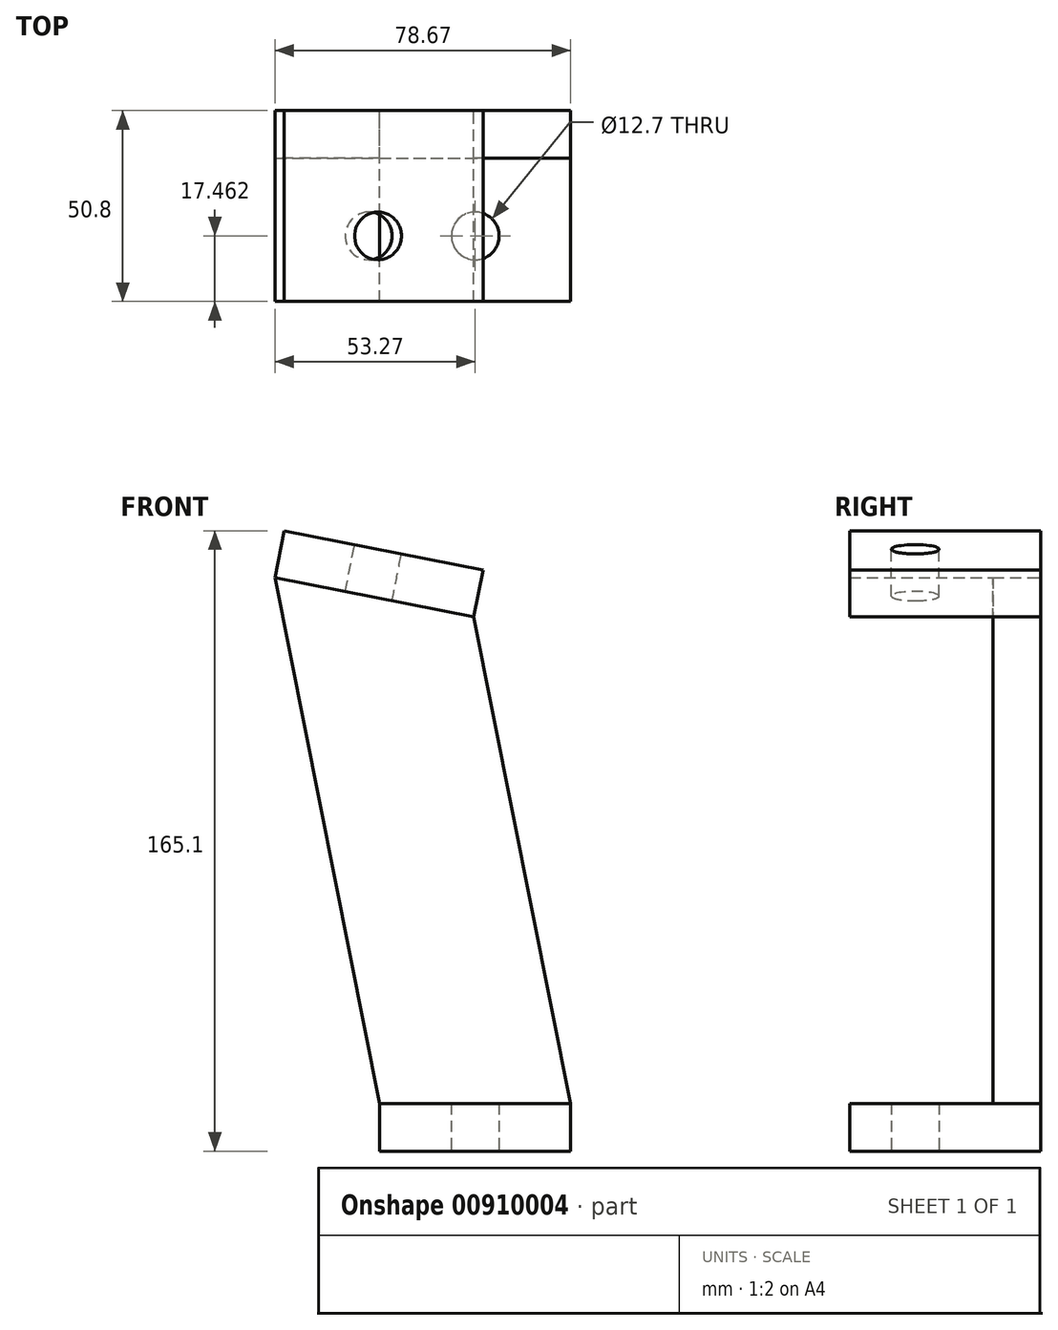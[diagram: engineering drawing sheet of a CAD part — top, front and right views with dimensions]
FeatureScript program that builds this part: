
annotation { "Feature Type Name" : "Feature", "Feature Type Description" : "" }
export const myFeature = defineFeature(function(context is Context, id is Id, definition is map)
    precondition{}
    {
        {
            var Q0;
            Q0=qCreatedBy(makeId("Front.planeOp"),FACE);
            var sketch = newSketch(context, id + "F0", { "sketchPlane" : qUnion([Q0])});
            skLineSegment(sketch, "E0.bottom", {"start": v(-25.4, 0) * mm, "end": v(25.4, 0) * mm});
            skLineSegment(sketch, "E0.top", {"start": v(-25.4, 12.7) * mm, "end": v(25.4, 12.7) * mm});
            skLineSegment(sketch, "E0.left", {"start": v(-25.4, 0) * mm, "end": v(-25.4, 12.7) * mm});
            skLineSegment(sketch, "E0.right", {"start": v(25.4, 0) * mm, "end": v(25.4, 12.7) * mm});
            skLineSegment(sketch, "E1", {"start": v(25.4, 12.7) * mm, "end": v(-0.38, 142.17) * mm});
            skLineSegment(sketch, "E2", {"start": v(-25.4, 12.7) * mm, "end": v(-53.27, 152.64) * mm});
            skLineSegment(sketch, "E3", {"start": v(-53.27, 152.64) * mm, "end": v(-0.38, 142.17) * mm});
            skLineSegment(sketch, "E4", {"start": v(-53.27, 152.64) * mm, "end": v(-50.8, 165.1) * mm});
            skLineSegment(sketch, "E5", {"start": v(-50.8, 165.1) * mm, "end": v(2.09, 154.62) * mm});
            skLineSegment(sketch, "E6", {"start": v(2.09, 154.62) * mm, "end": v(-0.38, 142.17) * mm});
            skSolve(sketch);
        }
        {
            var Q0;
            Q0=makeQuery(id+"F0.imprint","IMPRINT",FACE,{"disambiguationData":[TD([[makeQuery(id+"F0.imprint","IMPRINT",EDGE,{"derivedFrom":sQuery(id+"F0.wireOp",EDGE,"E0.bottom")}),1.0]])]});
            var Q1;
            Q1=makeQuery(id+"F0.imprint","IMPRINT",FACE,{"disambiguationData":[TD([[makeQuery(id+"F0.imprint","IMPRINT",EDGE,{"derivedFrom":sQuery(id+"F0.wireOp",EDGE,"E3")}),1.0]])]});
            extrude(context, id + "F1", {"entities" : qUnion([Q0, Q1]), "depth" : 50.8 * mm, "offsetDistance" : 25 * mm});
        }
        {
            var Q0;
            Q0=makeQuery(id+"F0.imprint","IMPRINT",FACE,{"disambiguationData":[TD([[makeQuery(id+"F0.imprint","IMPRINT",EDGE,{"derivedFrom":sQuery(id+"F0.wireOp",EDGE,"E0.top")}),1.0]])]});
            extrude(context, id + "F2", {"entities" : qUnion([Q0]), "operationType" : NewBodyOperationType.ADD, "depth" : 12.7 * mm, "offsetDistance" : 25 * mm});
        }
        {
            var Q0;
            Q0=makeQuery(id+"F1.opExtrude","SWEPT_FACE",FACE,{"disambiguationData":[OSD([sQuery(id+"F0.wireOp",EDGE,"E0.bottom")])]});
            var sketch = newSketch(context, id + "F3", { "sketchPlane" : qUnion([Q0])});
            skPoint(sketch, "E7", {"position": v(0, 33.34) * mm});
            skCircle(sketch, "E8", {"center": v(0, 33.34) * mm, "radius": 6.35 * mm});
            skSolve(sketch);
        }
        {
            var Q0;
            Q0=makeQuery(id+"F3.imprint","IMPRINT",FACE,{"disambiguationData":[TD([[makeQuery(id+"F3.imprint","IMPRINT",EDGE,{"derivedFrom":sQuery(id+"F3.wireOp",EDGE,"E8")}),1.0]])]});
            var Q1;
            Q1=makeQuery(id+"F1.opExtrude","SWEPT_FACE",FACE,{"disambiguationData":[OSD([sQuery(id+"F0.wireOp",EDGE,"E0.top")])]});
            extrude(context, id + "F4", {"entities" : qUnion([Q0]), "operationType" : NewBodyOperationType.REMOVE, "endBound" : BoundingType.UP_TO_SURFACE, "oppositeDirection" : true, "depth" : 25 * mm, "endBoundEntityFace" : qUnion([Q1]), "offsetDistance" : 25 * mm});
        }
        {
            var Q0;
            Q0=makeQuery(id+"F1.opExtrude","SWEPT_FACE",FACE,{"disambiguationData":[OSD([sQuery(id+"F0.wireOp",EDGE,"E5")])]});
            var sketch = newSketch(context, id + "F5", { "sketchPlane" : qUnion([Q0])});
            skCircle(sketch, "E9", {"center": v(-56.51, -33.34) * mm, "radius": 6.35 * mm});
            skSolve(sketch);
        }
        {
            var Q0;
            Q0=makeQuery(id+"F5.imprint","IMPRINT",FACE,{"disambiguationData":[TD([[makeQuery(id+"F5.imprint","IMPRINT",EDGE,{"derivedFrom":sQuery(id+"F5.wireOp",EDGE,"E9")}),1.0]])]});
            extrude(context, id + "F6", {"entities" : qUnion([Q0]), "operationType" : NewBodyOperationType.REMOVE, "endBound" : BoundingType.UP_TO_NEXT, "oppositeDirection" : true, "depth" : 25 * mm, "offsetDistance" : 25 * mm});
        }
    });
